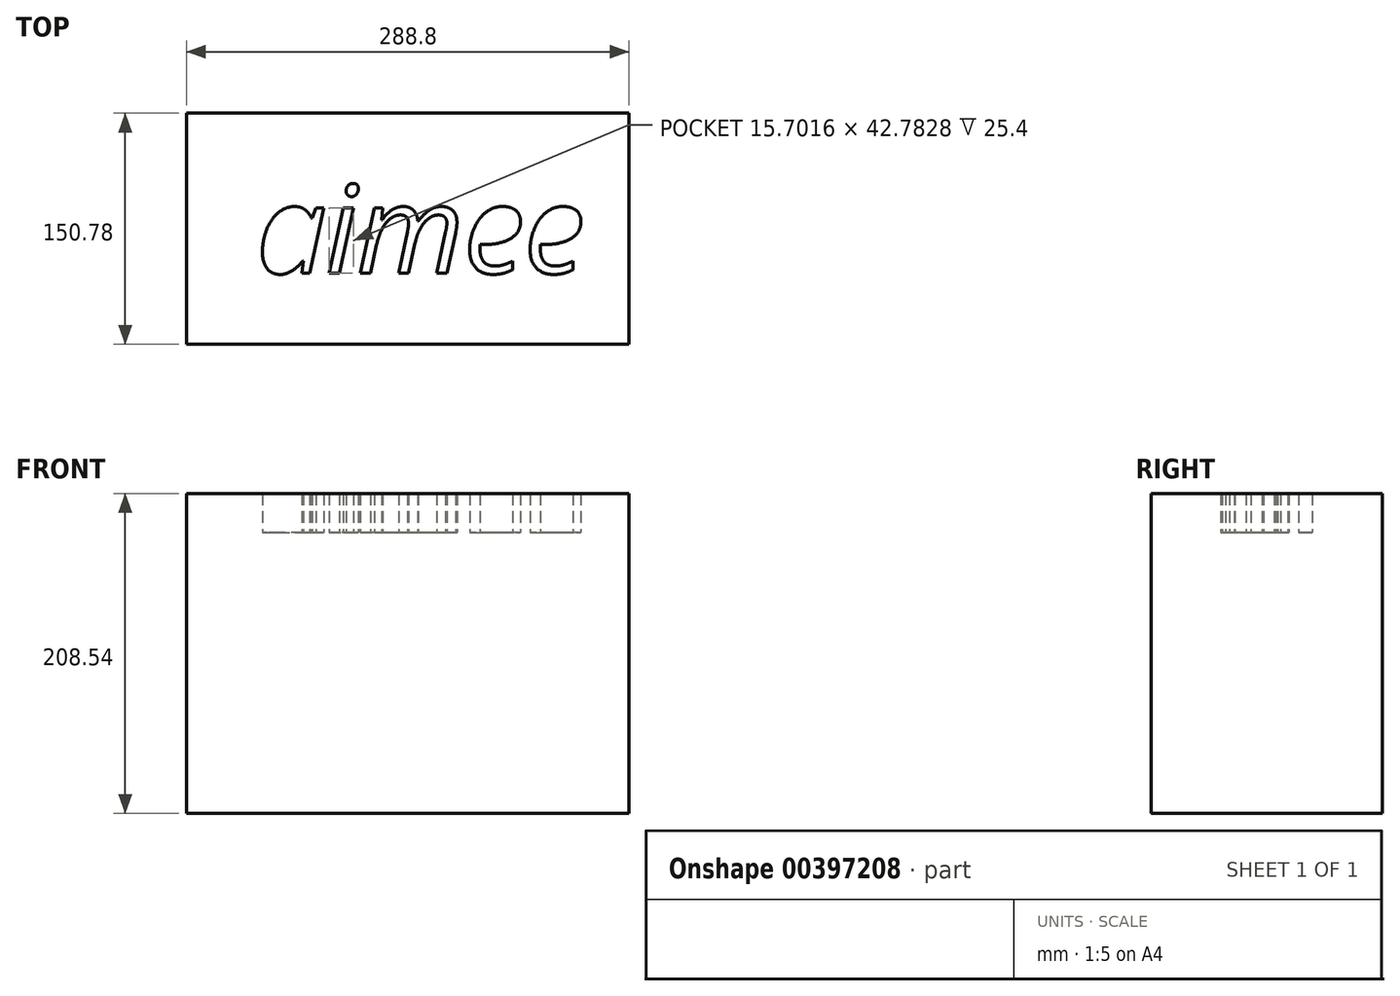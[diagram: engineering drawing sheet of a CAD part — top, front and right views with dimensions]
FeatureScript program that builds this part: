
annotation { "Feature Type Name" : "Feature", "Feature Type Description" : "" }
export const myFeature = defineFeature(function(context is Context, id is Id, definition is map)
    precondition{}
    {
        {
            var Q0;
            Q0=qCreatedBy(makeId("Right.planeOp"),FACE);
            var sketch = newSketch(context, id + "F0", { "sketchPlane" : qUnion([Q0])});
            skLineSegment(sketch, "E0.bottom", {"start": v(-32.38, 2.77) * mm, "end": v(-183.16, 2.77) * mm});
            skLineSegment(sketch, "E0.top", {"start": v(-32.38, 185.9) * mm, "end": v(-183.16, 185.9) * mm});
            skLineSegment(sketch, "E0.left", {"start": v(-32.38, 2.77) * mm, "end": v(-32.38, 185.9) * mm});
            skLineSegment(sketch, "E0.right", {"start": v(-183.16, 2.77) * mm, "end": v(-183.16, 185.9) * mm});
            skSolve(sketch);
        }
        {
            var Q0;
            Q0=makeQuery(id+"F0.imprint","IMPRINT",FACE,{"disambiguationData":[TD([[makeQuery(id+"F0.imprint","IMPRINT",EDGE,{"derivedFrom":sQuery(id+"F0.wireOp",EDGE,"E0.bottom")}),-1.0]])]});
            extrude(context, id + "F1", {"entities" : qUnion([Q0]), "depth" : 288.8 * mm});
        }
        {
            var Q0;
            Q0=makeQuery(id+"F1.opExtrude","SWEPT_FACE",FACE,{"disambiguationData":[OSD([sQuery(id+"F0.wireOp",EDGE,"E0.top")])]});
            var sketch = newSketch(context, id + "F2", { "sketchPlane" : qUnion([Q0])});
            skText(sketch, "E1", { "text": "aimee", "fontName": "OpenSans-Italic.ttf"});
            const initialGuessF2  = {"E1": [0.04575, -0.1369, 1, 0, 0.05756]};
            skSetInitialGuess(sketch, initialGuessF2);
            skSolve(sketch);
        }
        {
            var Q0;
            Q0=makeQuery(id+"F2.imprint","IMPRINT",FACE,{"disambiguationData":[TD([[makeQuery(id+"F2.imprint","IMPRINT",EDGE,{"derivedFrom":sQuery(id+"F2.wireOp",EDGE,"E1.sketch_text.stroke-0")}),1.0]])]});
            extrude(context, id + "F3", {"entities" : qUnion([Q0]), "operationType" : NewBodyOperationType.ADD, "depth" : 25.4 * mm});
        }
    });
